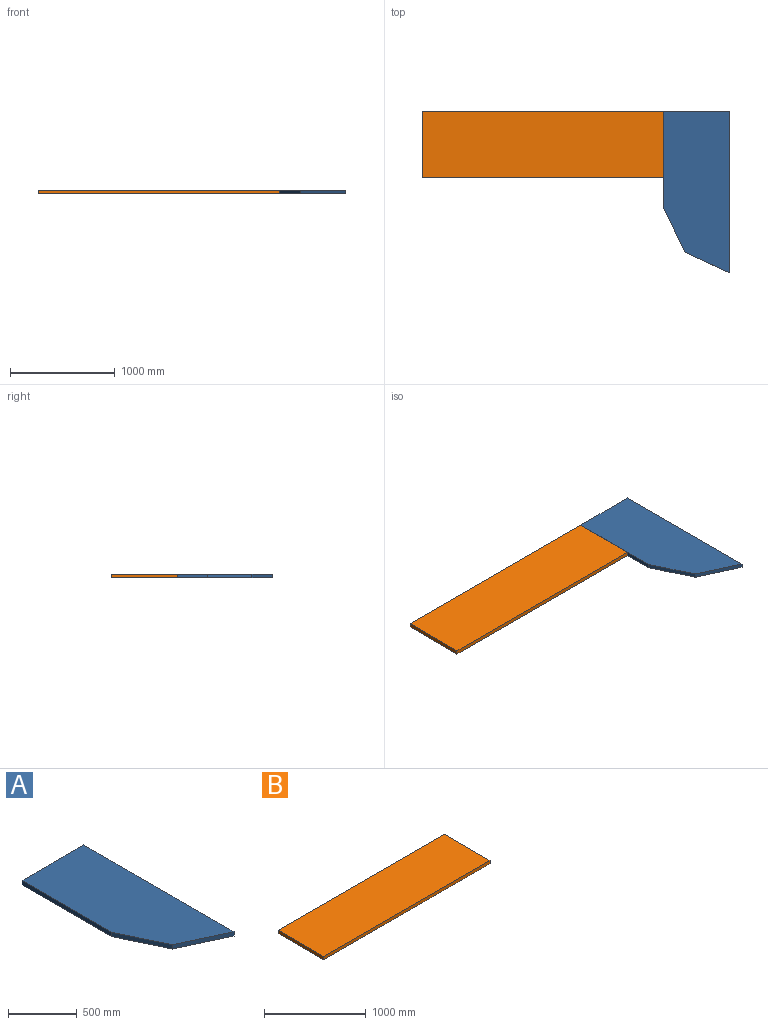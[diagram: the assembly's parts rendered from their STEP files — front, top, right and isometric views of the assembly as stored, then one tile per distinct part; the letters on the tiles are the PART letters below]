
ASSEMBLY  parts=2 mates=1
PART A: 7 faces, bbox 635x1546.2x38.1 mm
  f0: plane 920.75x38.1mm, normal (-1,0,0), area 35080.6mm2, adj f1,f4,f5,f6
  f1: plane 425.45x203.2mm, normal (-0.9,-0.43,0), area 17963.6mm2, adj f0,f2,f5,f6
  f2: plane 431.8x200.03mm, normal (-0.42,-0.91,0), area 18131mm2, adj f1,f3,f5,f6
  f3: plane 1546.23x38.1mm, normal (1,0,0), area 58911.2mm2, adj f2,f4,f5,f6
  f4: plane 635x38.1mm, normal (0,1,0), area 24193.5mm2, adj f0,f3,f5,f6
  f5: plane 1546.23x635mm, normal (0,0,1), area 854796.7mm2, adj f0,f1,f2,f3,f4
  f6: plane 1546.23x635mm, normal (0,0,-1), area 854796.7mm2, adj f0,f1,f2,f3,f4
PART B: 6 faces, bbox 2305.1x635x38.1 mm
  f0: plane 2305.05x38.1mm, normal (0,-1,0), area 87822.4mm2, adj f1,f3,f4,f5
  f1: plane 635x38.1mm, normal (1,0,0), area 24193.5mm2, adj f0,f2,f4,f5
  f2: plane 2305.05x38.1mm, normal (0,1,0), area 87822.4mm2, adj f1,f3,f4,f5
  f3: plane 635x38.1mm, normal (-1,0,0), area 24193.5mm2, adj f0,f2,f4,f5
  f4: plane 2305.05x635mm, normal (0,0,1), area 1463706.8mm2, adj f0,f1,f2,f3
  f5: plane 2305.05x635mm, normal (0,0,-1), area 1463706.8mm2, adj f0,f1,f2,f3
PLACE A t=(1948.79,1921.1,231.41)mm
PLACE B t=(-356.26,1286.1,231.41)mm
MATE fastened A.f5 <-> B.f4  axis (0,0,1) through (1948.79,1921.1,269.51)mm
